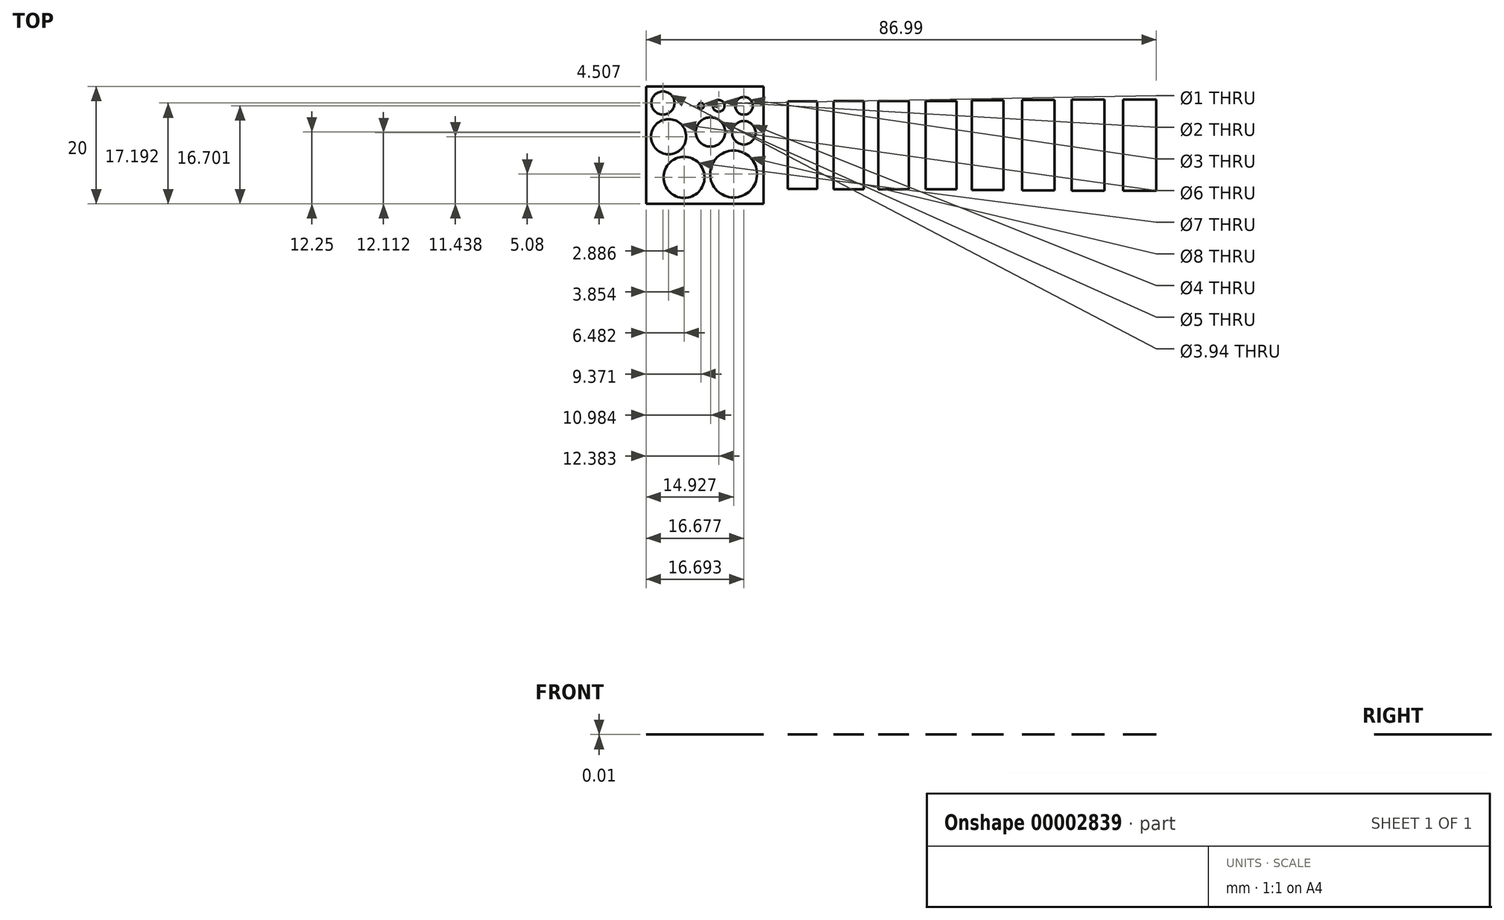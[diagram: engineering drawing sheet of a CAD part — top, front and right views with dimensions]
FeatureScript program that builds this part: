
annotation { "Feature Type Name" : "Feature", "Feature Type Description" : "" }
export const myFeature = defineFeature(function(context is Context, id is Id, definition is map)
    precondition{}
    {
        {
            var Q0;
            Q0=qCreatedBy(makeId("Top.planeOp"),FACE);
            var sketch = newSketch(context, id + "F0", { "sketchPlane" : qUnion([Q0])});
            skLineSegment(sketch, "E0.rect.bottom", {"start": v(-10, 10) * mm, "end": v(10, 10) * mm});
            skLineSegment(sketch, "E0.rect.top", {"start": v(-10, -10) * mm, "end": v(10, -10) * mm});
            skLineSegment(sketch, "E0.rect.left", {"start": v(-10, 10) * mm, "end": v(-10, -10) * mm});
            skLineSegment(sketch, "E0.rect.right", {"start": v(10, 10) * mm, "end": v(10, -10) * mm});
            skPoint(sketch, "E0.rect.middle", {"position": v(0, 0) * mm});
            skCircle(sketch, "E1", {"center": v(-0.63, 6.7) * mm, "radius": 0.5 * mm});
            skCircle(sketch, "E2", {"center": v(2.38, 6.7) * mm, "radius": 1 * mm});
            skCircle(sketch, "E3", {"center": v(6.7, 6.7) * mm, "radius": 1.5 * mm});
            skCircle(sketch, "E4", {"center": v(-6.15, 1.44) * mm, "radius": 3 * mm});
            skCircle(sketch, "E5", {"center": v(-3.52, -5.5) * mm, "radius": 3.5 * mm});
            skCircle(sketch, "E6", {"center": v(4.93, -4.92) * mm, "radius": 4 * mm});
            skCircle(sketch, "E7", {"center": v(6.68, 2.11) * mm, "radius": 2 * mm});
            skCircle(sketch, "E8", {"center": v(0.98, 2.25) * mm, "radius": 2.5 * mm});
            skCircle(sketch, "E9", {"center": v(-7.11, 7.2) * mm, "radius": 1.97 * mm});
            skLineSegment(sketch, "E10.rect.bottom", {"start": v(14.15, 7.45) * mm, "end": v(19.15, 7.45) * mm});
            skLineSegment(sketch, "E10.rect.top", {"start": v(14.15, -7.45) * mm, "end": v(19.15, -7.45) * mm});
            skLineSegment(sketch, "E10.rect.left", {"start": v(14.15, 7.45) * mm, "end": v(14.15, -7.45) * mm});
            skLineSegment(sketch, "E10.rect.right", {"start": v(19.15, 7.45) * mm, "end": v(19.15, -7.45) * mm});
            skPoint(sketch, "E10.rect.middle", {"position": v(16.65, 0) * mm});
            skLineSegment(sketch, "E11.rect.bottom", {"start": v(21.98, 7.5) * mm, "end": v(27.08, 7.5) * mm});
            skLineSegment(sketch, "E11.rect.top", {"start": v(21.98, -7.5) * mm, "end": v(27.08, -7.5) * mm});
            skLineSegment(sketch, "E11.rect.left", {"start": v(21.98, 7.5) * mm, "end": v(21.98, -7.5) * mm});
            skLineSegment(sketch, "E11.rect.right", {"start": v(27.08, 7.5) * mm, "end": v(27.08, -7.5) * mm});
            skPoint(sketch, "E11.rect.middle", {"position": v(24.53, 0) * mm});
            skLineSegment(sketch, "E12.rect.bottom", {"start": v(29.6, 7.55) * mm, "end": v(34.8, 7.55) * mm});
            skLineSegment(sketch, "E12.rect.top", {"start": v(29.6, -7.55) * mm, "end": v(34.8, -7.55) * mm});
            skLineSegment(sketch, "E12.rect.left", {"start": v(29.6, 7.55) * mm, "end": v(29.6, -7.55) * mm});
            skLineSegment(sketch, "E12.rect.right", {"start": v(34.8, 7.55) * mm, "end": v(34.8, -7.55) * mm});
            skPoint(sketch, "E12.rect.middle", {"position": v(32.2, 0) * mm});
            skLineSegment(sketch, "E13.rect.bottom", {"start": v(37.63, 7.55) * mm, "end": v(42.93, 7.55) * mm});
            skLineSegment(sketch, "E13.rect.top", {"start": v(37.63, -7.55) * mm, "end": v(42.93, -7.55) * mm});
            skLineSegment(sketch, "E13.rect.left", {"start": v(37.63, 7.55) * mm, "end": v(37.63, -7.65) * mm});
            skLineSegment(sketch, "E13.rect.right", {"start": v(42.93, 7.55) * mm, "end": v(42.93, -7.55) * mm});
            skPoint(sketch, "E13.rect.middle", {"position": v(40.28, 0) * mm});
            skLineSegment(sketch, "E14.rect.bottom", {"start": v(45.54, 7.65) * mm, "end": v(50.94, 7.65) * mm});
            skLineSegment(sketch, "E14.rect.top", {"start": v(45.54, -7.65) * mm, "end": v(50.94, -7.65) * mm});
            skLineSegment(sketch, "E14.rect.left", {"start": v(45.54, 7.65) * mm, "end": v(45.54, -7.65) * mm});
            skLineSegment(sketch, "E14.rect.right", {"start": v(50.94, 7.65) * mm, "end": v(50.94, -7.65) * mm});
            skPoint(sketch, "E14.rect.middle", {"position": v(48.24, 0) * mm});
            skLineSegment(sketch, "E15.rect.bottom", {"start": v(54.13, 7.7) * mm, "end": v(59.63, 7.7) * mm});
            skLineSegment(sketch, "E15.rect.top", {"start": v(54.13, -7.7) * mm, "end": v(59.63, -7.7) * mm});
            skLineSegment(sketch, "E15.rect.left", {"start": v(54.13, 7.7) * mm, "end": v(54.13, -7.7) * mm});
            skLineSegment(sketch, "E15.rect.right", {"start": v(59.63, 7.7) * mm, "end": v(59.63, -7.7) * mm});
            skPoint(sketch, "E15.rect.middle", {"position": v(56.88, 0) * mm});
            skLineSegment(sketch, "E16.rect.bottom", {"start": v(62.54, 7.75) * mm, "end": v(68.14, 7.75) * mm});
            skLineSegment(sketch, "E16.rect.top", {"start": v(62.54, -7.75) * mm, "end": v(68.14, -7.75) * mm});
            skLineSegment(sketch, "E16.rect.left", {"start": v(62.54, 7.75) * mm, "end": v(62.54, -7.75) * mm});
            skLineSegment(sketch, "E16.rect.right", {"start": v(68.14, 7.75) * mm, "end": v(68.14, -7.75) * mm});
            skPoint(sketch, "E16.rect.middle", {"position": v(65.34, 0) * mm});
            skLineSegment(sketch, "E17.rect.bottom", {"start": v(71.3, 7.8) * mm, "end": v(77, 7.8) * mm});
            skLineSegment(sketch, "E17.rect.top", {"start": v(71.3, -7.8) * mm, "end": v(77, -7.8) * mm});
            skLineSegment(sketch, "E17.rect.left", {"start": v(71.3, 7.8) * mm, "end": v(71.3, -7.8) * mm});
            skLineSegment(sketch, "E17.rect.right", {"start": v(77, 7.8) * mm, "end": v(77, -7.8) * mm});
            skPoint(sketch, "E17.rect.middle", {"position": v(74.14, 0) * mm});
            skSolve(sketch);
        }
        {
            var Q0;
            Q0 = qSketchRegion(id + "F0", true);
            extrude(context, id + "F1", {"entities" : qUnion([Q0]), "depth" : 3 / 406.4 * mm});
        }
    });
